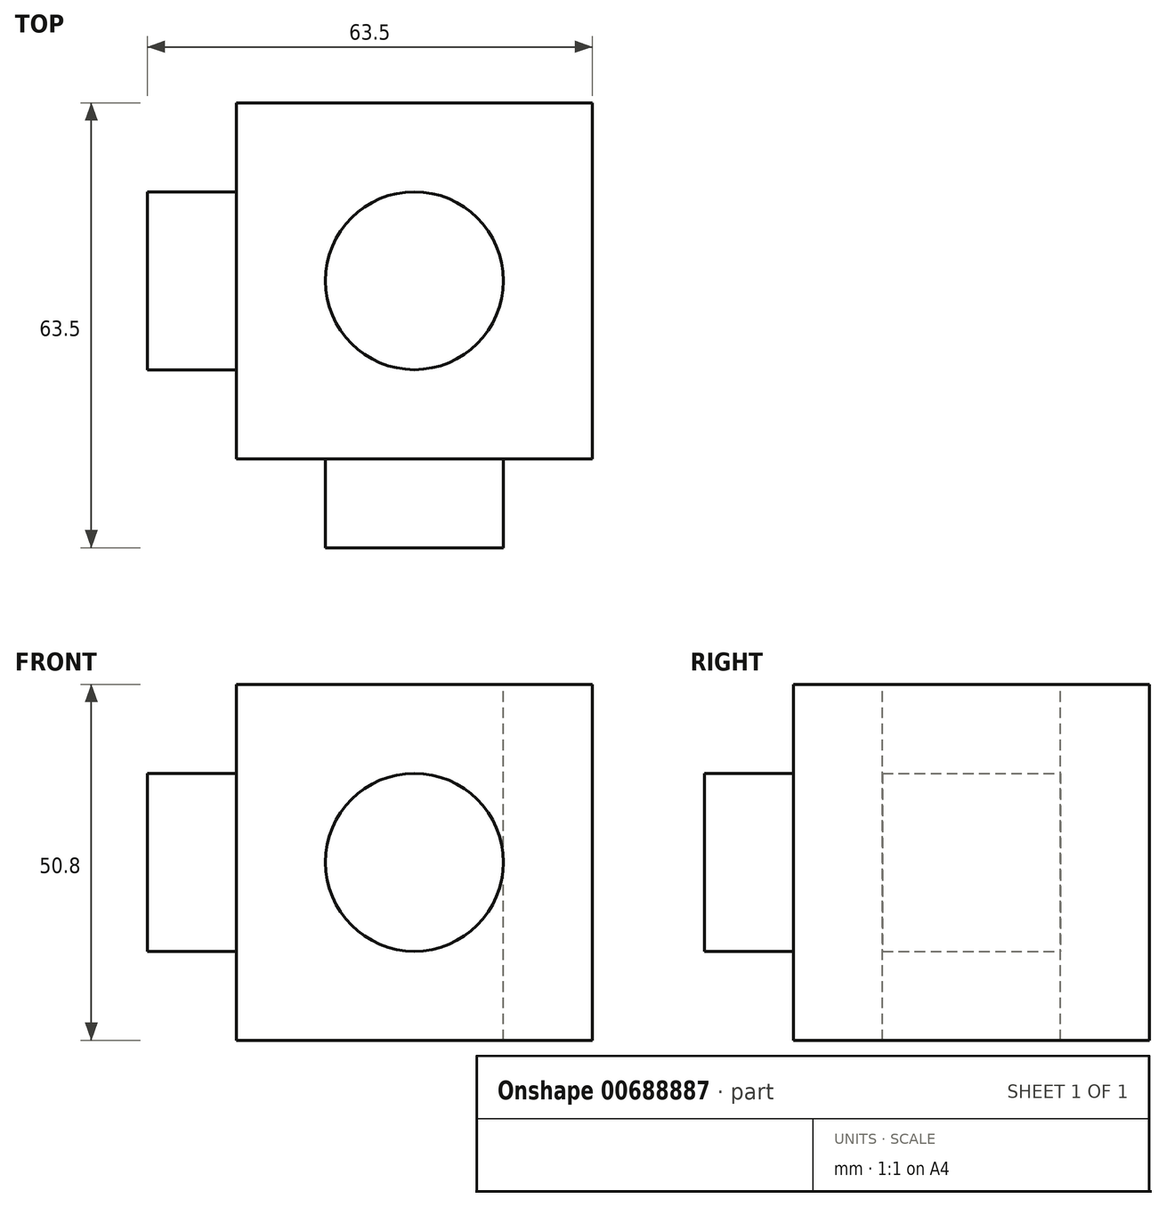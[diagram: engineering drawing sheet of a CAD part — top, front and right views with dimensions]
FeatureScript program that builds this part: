
annotation { "Feature Type Name" : "Feature", "Feature Type Description" : "" }
export const myFeature = defineFeature(function(context is Context, id is Id, definition is map)
    precondition{}
    {
        {
            var Q0;
            Q0=qCreatedBy(makeId("Front.planeOp"),FACE);
            var sketch = newSketch(context, id + "F0", { "sketchPlane" : qUnion([Q0])});
            skLineSegment(sketch, "E0.bottom", {"start": v(25.4, 25.4) * mm, "end": v(-25.4, 25.4) * mm});
            skLineSegment(sketch, "E0.top", {"start": v(25.4, -25.4) * mm, "end": v(-25.4, -25.4) * mm});
            skLineSegment(sketch, "E0.left", {"start": v(25.4, 25.4) * mm, "end": v(25.4, -25.4) * mm});
            skLineSegment(sketch, "E0.right", {"start": v(-25.4, 25.4) * mm, "end": v(-25.4, -25.4) * mm});
            skPoint(sketch, "E0.middle", {"position": v(0, 0) * mm});
            skSolve(sketch);
        }
        {
            var Q0;
            Q0 = qSketchRegion(id + "F0", true);
            extrude(context, id + "F1", {"entities" : qUnion([Q0]), "depth" : 50.8 * mm, "offsetDistance" : 25.4 * mm});
        }
        {
            var Q0;
            Q0=makeQuery(id+"F1.opExtrude","SWEPT_FACE",FACE,{"disambiguationData":[OSD([sQuery(id+"F0.wireOp",EDGE,"E0.bottom")])]});
            var sketch = newSketch(context, id + "F2", { "sketchPlane" : qUnion([Q0])});
            skCircle(sketch, "E1", {"center": v(0, -25.4) * mm, "radius": 12.7 * mm});
            skPoint(sketch, "E1.centerSnap0", {"position": v(-25.4, -25.4) * mm});
            skPoint(sketch, "E1.centerSnap1", {"position": v(0, -50.8) * mm});
            skSolve(sketch);
        }
        {
            var Q0;
            Q0 = qSketchRegion(id + "F2", true);
            extrude(context, id + "F3", {"entities" : qUnion([Q0]), "operationType" : NewBodyOperationType.REMOVE, "oppositeDirection" : true, "depth" : 50.8 * mm, "offsetDistance" : 25.4 * mm});
        }
        {
            var Q0;
            Q0=makeQuery(id+"F1.opExtrude","CAP_FACE",FACE,{"disambiguationData":[OSD([sQuery(id+"F0.wireOp",EDGE,"E0.bottom"),sQuery(id+"F0.wireOp",EDGE,"E0.top"),sQuery(id+"F0.wireOp",EDGE,"E0.left"),sQuery(id+"F0.wireOp",EDGE,"E0.right")])],"isStart":false});
            var sketch = newSketch(context, id + "F4", { "sketchPlane" : qUnion([Q0])});
            skCircle(sketch, "E2", {"center": v(0, 0) * mm, "radius": 12.7 * mm});
            skSolve(sketch);
        }
        {
            var Q0;
            Q0 = qSketchRegion(id + "F4", true);
            extrude(context, id + "F5", {"entities" : qUnion([Q0]), "operationType" : NewBodyOperationType.ADD, "depth" : 12.7 * mm, "offsetDistance" : 25.4 * mm});
        }
        {
            var Q0;
            Q0=makeQuery(id+"F1.opExtrude","SWEPT_FACE",FACE,{"disambiguationData":[OSD([sQuery(id+"F0.wireOp",EDGE,"E0.right")])]});
            var sketch = newSketch(context, id + "F6", { "sketchPlane" : qUnion([Q0])});
            skLineSegment(sketch, "E3.bottom", {"start": v(38.1, 12.7) * mm, "end": v(12.7, 12.7) * mm});
            skLineSegment(sketch, "E3.top", {"start": v(38.1, -12.7) * mm, "end": v(12.7, -12.7) * mm});
            skLineSegment(sketch, "E3.left", {"start": v(38.1, 12.7) * mm, "end": v(38.1, -12.7) * mm});
            skLineSegment(sketch, "E3.right", {"start": v(12.7, 12.7) * mm, "end": v(12.7, -12.7) * mm});
            skPoint(sketch, "E3.middle", {"position": v(25.4, 0) * mm});
            skPoint(sketch, "E3.middle.positionSnap0", {"position": v(25.4, 25.4) * mm});
            skPoint(sketch, "E3.centerSnap0", {"position": v(25.4, 25.4) * mm});
            skSolve(sketch);
        }
        {
            var Q0;
            Q0 = qSketchRegion(id + "F6", true);
            extrude(context, id + "F7", {"entities" : qUnion([Q0]), "operationType" : NewBodyOperationType.ADD, "depth" : 12.7 * mm, "offsetDistance" : 25.4 * mm});
        }
    });
